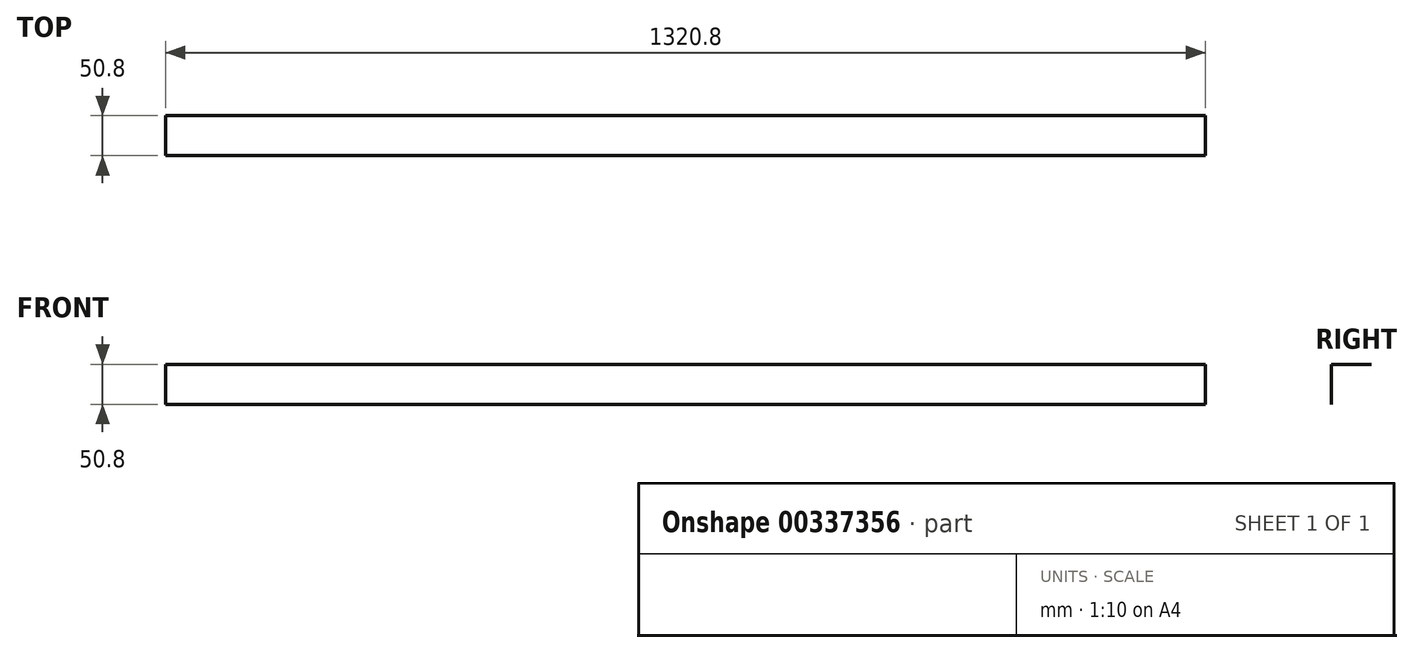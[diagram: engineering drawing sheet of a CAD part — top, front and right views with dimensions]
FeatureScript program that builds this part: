
annotation { "Feature Type Name" : "Feature", "Feature Type Description" : "" }
export const myFeature = defineFeature(function(context is Context, id is Id, definition is map)
    precondition{}
    {
        {
            var Q0;
            Q0=qCreatedBy(makeId("Right.planeOp"),FACE);
            var sketch = newSketch(context, id + "F0", { "sketchPlane" : qUnion([Q0])});
            skLineSegment(sketch, "E0", {"start": v(-50.8, -69.54) * mm, "end": v(-50.8, -18.74) * mm});
            skLineSegment(sketch, "E1", {"start": v(-50.8, -18.74) * mm, "end": v(0, -18.74) * mm});
            skSolve(sketch);
        }
        {
            var Q0;
            Q0 = qSketchRegion(id + "F0", true);
            var Q1;
            Q1=sQuery(id+"F0.wireOp",EDGE,"E1");
            var Q2;
            Q2=sQuery(id+"F0.wireOp",EDGE,"E0");
            extrude(context, id + "F1", {"entities" : qUnion([Q0]), "bodyType" : ToolBodyType.SURFACE, "surfaceEntities" : qUnion([Q1, Q2]), "depth" : 1320.8 * mm});
        }
    });
